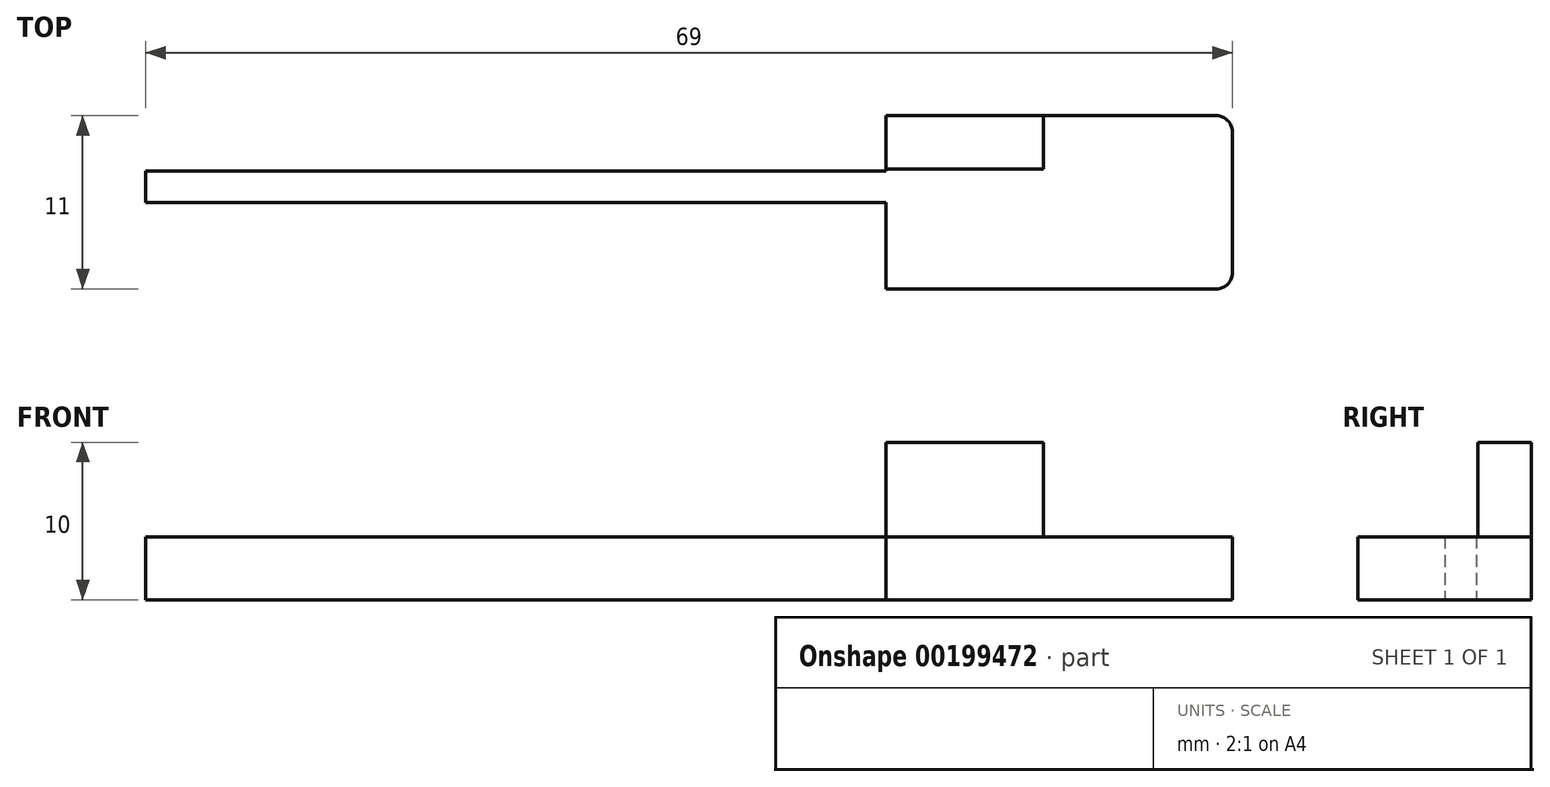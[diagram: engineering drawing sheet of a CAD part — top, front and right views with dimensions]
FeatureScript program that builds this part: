
annotation { "Feature Type Name" : "Feature", "Feature Type Description" : "" }
export const myFeature = defineFeature(function(context is Context, id is Id, definition is map)
    precondition{}
    {
        {
            var Q0;
            Q0=qCreatedBy(makeId("Top.planeOp"),FACE);
            var sketch = newSketch(context, id + "F0", { "sketchPlane" : qUnion([Q0])});
            skLineSegment(sketch, "E0.bottom", {"start": v(-36.1, 10.56) * mm, "end": v(10.9, 10.56) * mm});
            skLineSegment(sketch, "E0.top", {"start": v(-36.1, 8.56) * mm, "end": v(10.9, 8.56) * mm});
            skLineSegment(sketch, "E0.left", {"start": v(-36.1, 10.56) * mm, "end": v(-36.1, 8.56) * mm});
            skLineSegment(sketch, "E0.right", {"start": v(10.9, 10.56) * mm, "end": v(10.9, 8.56) * mm});
            skLineSegment(sketch, "E1.bottom", {"start": v(32.9, 14.06) * mm, "end": v(10.9, 14.06) * mm});
            skLineSegment(sketch, "E1.top", {"start": v(32.9, 3.06) * mm, "end": v(10.9, 3.06) * mm});
            skLineSegment(sketch, "E1.left", {"start": v(32.9, 14.06) * mm, "end": v(32.9, 3.06) * mm});
            skLineSegment(sketch, "E1.right", {"start": v(10.9, 14.06) * mm, "end": v(10.9, 3.06) * mm});
            skLineSegment(sketch, "E2.bottom", {"start": v(10.9, 10.66) * mm, "end": v(20.9, 10.66) * mm});
            skLineSegment(sketch, "E2.top", {"start": v(10.9, 14.06) * mm, "end": v(20.9, 14.06) * mm});
            skLineSegment(sketch, "E2.left", {"start": v(10.9, 10.66) * mm, "end": v(10.9, 14.06) * mm});
            skLineSegment(sketch, "E2.right", {"start": v(20.9, 10.66) * mm, "end": v(20.9, 14.06) * mm});
            skSolve(sketch);
        }
        {
            var Q0;
            {var subQ0=sQuery(id+"F0.wireOp",EDGE,"E0.left");Q0=makeQuery(id+"F0.imprint","IMPRINT",FACE,{"disambiguationData":[TD([[makeQuery(id+"F0.imprint","IMPRINT",EDGE,{"derivedFrom":subQ0}),1.0]])]});}
            var Q1;
            {var subQ0=sQuery(id+"F0.wireOp",EDGE,"E0.right");Q1=makeQuery(id+"F0.imprint","IMPRINT",FACE,{"disambiguationData":[TD([[makeQuery(id+"F0.imprint","IMPRINT",EDGE,{"derivedFrom":subQ0}),-1.0]])]});}
            var Q2;
            {var subQ0=sQuery(id+"F0.wireOp",EDGE,"E0.right");Q2=makeQuery(id+"F0.imprint","IMPRINT",FACE,{"disambiguationData":[TD([[makeQuery(id+"F0.imprint","IMPRINT",EDGE,{"derivedFrom":subQ0}),1.0]])]});}
            var Q3;
            Q3=makeQuery(id+"F0.imprint","IMPRINT",FACE,{"disambiguationData":[TD([[makeQuery(id+"F0.imprint","IMPRINT",EDGE,{"derivedFrom":sQuery(id+"F0.wireOp",EDGE,"E2.bottom")}),1.0]])]});
            var Q4;
            Q4=makeQuery(id+"F0.imprint","IMPRINT",FACE,{"disambiguationData":[TD([[makeQuery(id+"F0.imprint","IMPRINT",EDGE,{"derivedFrom":sQuery(id+"F0.wireOp",EDGE,"E1.bottom")}),1.0]])]});
            extrude(context, id + "F1", {"entities" : qUnion([Q0, Q1, Q2, Q3, Q4]), "depth" : 4 * mm});
        }
        {
            var Q0;
            Q0=makeQuery(id+"F0.imprint","IMPRINT",FACE,{"disambiguationData":[TD([[makeQuery(id+"F0.imprint","IMPRINT",EDGE,{"derivedFrom":sQuery(id+"F0.wireOp",EDGE,"E2.bottom")}),1.0]])]});
            extrude(context, id + "F2", {"entities" : qUnion([Q0]), "operationType" : NewBodyOperationType.ADD, "depth" : 10 * mm});
        }
        {
            var Q0;
            Q0=makeQuery(id+"F1.opExtrude","SWEPT_EDGE",EDGE,{"disambiguationData":[OSD([sQuery(id+"F0.wireOp",EDGE,"E1.top"),sQuery(id+"F0.wireOp",EDGE,"E1.left")])]});
            var Q1;
            Q1=makeQuery(id+"F1.opExtrude","SWEPT_EDGE",EDGE,{"disambiguationData":[OSD([sQuery(id+"F0.wireOp",EDGE,"E1.bottom"),sQuery(id+"F0.wireOp",EDGE,"E1.left")])]});
            fillet(context, id + "F3", {"entities" : qUnion([Q0, Q1]), "radius" : 1 * mm, "tangentPropagation" : true, "allowEdgeOverflow" : false});
        }
    });
